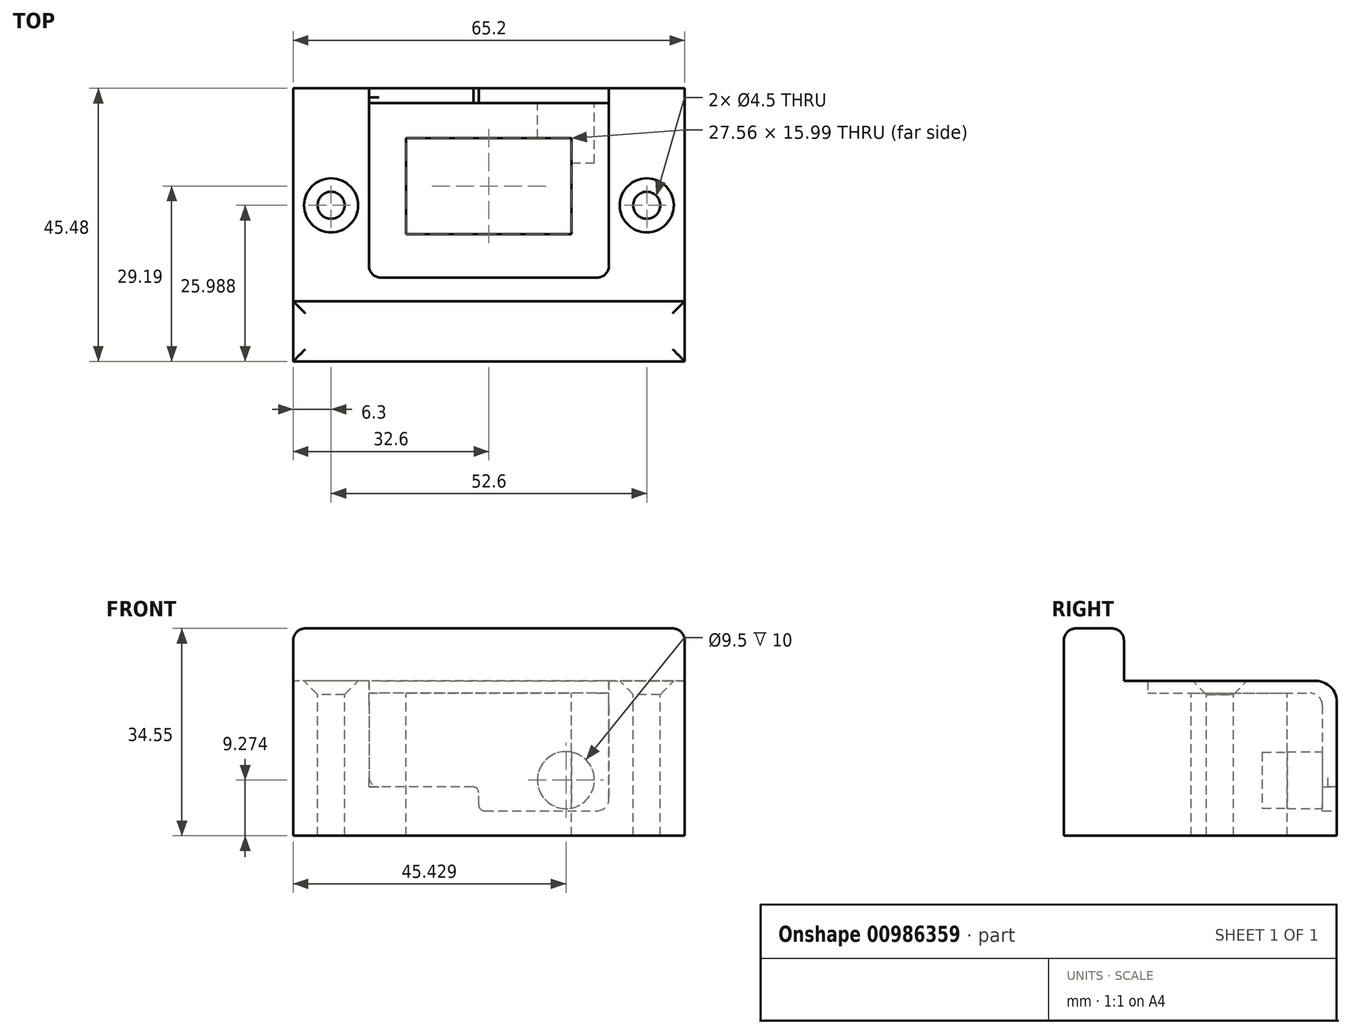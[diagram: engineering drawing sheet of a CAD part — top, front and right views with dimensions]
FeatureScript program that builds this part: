
annotation { "Feature Type Name" : "Feature", "Feature Type Description" : "" }
export const myFeature = defineFeature(function(context is Context, id is Id, definition is map)
    precondition{}
    {
        {
            var Q0;
            Q0=qCreatedBy(makeId("Right.planeOp"),FACE);
            var sketch = newSketch(context, id + "F0", { "sketchPlane" : qUnion([Q0])});
            skLineSegment(sketch, "E0.bottom", {"start": v(-15.25, 10.5) * mm, "end": v(15.25, 10.5) * mm});
            skLineSegment(sketch, "E0.top", {"start": v(13.85, -10.5) * mm, "end": v(15.25, -10.5) * mm});
            skLineSegment(sketch, "E0.left", {"start": v(-15.25, 10.5) * mm, "end": v(-15.25, 9.1) * mm});
            skLineSegment(sketch, "E0.right", {"start": v(15.25, 10.5) * mm, "end": v(15.25, -10.5) * mm});
            skPoint(sketch, "E0.middle", {"position": v(0, 0) * mm});
            skLineSegment(sketch, "E1.0", {"start": v(13.85, 9.1) * mm, "end": v(13.85, -10.5) * mm});
            skLineSegment(sketch, "E1.1", {"start": v(-15.25, 9.1) * mm, "end": v(13.85, 9.1) * mm});
            skPoint(sketch, "E2.orphan", {"position": v(-15.25, -10.5) * mm});
            skSolve(sketch);
        }
        {
            var Q0;
            Q0 = qSketchRegion(id + "F0", true);
            extrude(context, id + "F1", {"entities" : qUnion([Q0]), "endBound" : BoundingType.SYMMETRIC, "depth" : 40 * mm, "offsetDistance" : 25 * mm});
        }
        {
            var Q0;
            Q0=makeQuery(id+"F1.opExtrude","SWEPT_EDGE",EDGE,{"disambiguationData":[OSD([sQuery(id+"F0.wireOp",EDGE,"E1.0"),sQuery(id+"F0.wireOp",EDGE,"E1.1")])]});
            fillet(context, id + "F2", {"entities" : qUnion([Q0]), "radius" : 2 * mm, "tangentPropagation" : true, "allowEdgeOverflow" : false});
        }
        {
            var Q0;
            Q0=makeQuery(id+"F1.opExtrude","SWEPT_EDGE",EDGE,{"disambiguationData":[OSD([sQuery(id+"F0.wireOp",EDGE,"E0.bottom"),sQuery(id+"F0.wireOp",EDGE,"E0.right")])]});
            fillet(context, id + "F3", {"entities" : qUnion([Q0]), "radius" : 3 * mm, "tangentPropagation" : true, "allowEdgeOverflow" : false});
        }
        {
            var Q0;
            Q0=makeQuery(id+"F1.opExtrude","CAP_EDGE",EDGE,{"disambiguationData":[OSD([sQuery(id+"F0.wireOp",EDGE,"E0.top")])],"isStart":false});
            var Q1;
            Q1=makeQuery(id+"F1.opExtrude","CAP_EDGE",EDGE,{"disambiguationData":[OSD([sQuery(id+"F0.wireOp",EDGE,"E0.left")])],"isStart":false});
            var Q2;
            Q2=makeQuery(id+"F1.opExtrude","CAP_EDGE",EDGE,{"disambiguationData":[OSD([sQuery(id+"F0.wireOp",EDGE,"E0.left")])],"isStart":true});
            fillet(context, id + "F4", {"entities" : qUnion([Q0, Q1, Q2]), "radius" : 2 * mm, "tangentPropagation" : true, "allowEdgeOverflow" : false});
        }
        {
            var Q0;
            Q0=makeQuery(id+"F1.opExtrude","SWEPT_FACE",FACE,{"disambiguationData":[OSD([sQuery(id+"F0.wireOp",EDGE,"E0.right")])]});
            var sketch = newSketch(context, id + "F5", { "sketchPlane" : qUnion([Q0])});
            skLineSegment(sketch, "E3", {"start": v(20, -10.5) * mm, "end": v(0, -10.5) * mm});
            skLineSegment(sketch, "E4", {"start": v(0, -10.5) * mm, "end": v(0, -6.5) * mm});
            skLineSegment(sketch, "E5", {"start": v(0, -6.5) * mm, "end": v(20, -6.5) * mm});
            skLineSegment(sketch, "E6", {"start": v(20, -6.5) * mm, "end": v(20, -10.5) * mm});
            skSolve(sketch);
        }
        {
            var Q0;
            Q0 = qSketchRegion(id + "F5", true);
            extrude(context, id + "F6", {"entities" : qUnion([Q0]), "operationType" : NewBodyOperationType.REMOVE, "oppositeDirection" : true, "depth" : 8.3 * mm, "offsetDistance" : 25 * mm});
        }
        {
            var Q0;
            Q0=makeQuery(id+"F6.boolean.opBoolean","COPY",EDGE,{"derivedFrom":makeQuery(id+"F6.opExtrude","SWEPT_EDGE",EDGE,{"disambiguationData":[OSD([sQuery(id+"F0.wireOp",EDGE,"E0.right"),sQuery(id+"F5.wireOp",EDGE,"E5"),sQuery(id+"F5.wireOp",EDGE,"E6")])]})});
            var Q1;
            Q1=makeQuery(id+"F6.boolean.opBoolean","COPY",EDGE,{"derivedFrom":makeQuery(id+"F6.opExtrude","SWEPT_EDGE",EDGE,{"disambiguationData":[OSD([sQuery(id+"F0.wireOp",EDGE,"E0.top"),sQuery(id+"F0.wireOp",EDGE,"E0.right"),sQuery(id+"F5.wireOp",EDGE,"E3"),sQuery(id+"F5.wireOp",EDGE,"E4")])]})});
            var Q2;
            Q2=makeQuery(id+"F6.boolean.opBoolean","COPY",EDGE,{"derivedFrom":makeQuery(id+"F6.opExtrude","SWEPT_EDGE",EDGE,{"disambiguationData":[OSD([sQuery(id+"F5.wireOp",EDGE,"E4"),sQuery(id+"F5.wireOp",EDGE,"E5")])]})});
            fillet(context, id + "F7", {"entities" : qUnion([Q0, Q1, Q2]), "radius" : 1.69 * mm, "tangentPropagation" : true, "allowEdgeOverflow" : false});
        }
        {
            var Q0;
            Q0=qCreatedBy(makeId("Right.planeOp"),FACE);
            var sketch = newSketch(context, id + "F8", { "sketchPlane" : qUnion([Q0])});
            skLineSegment(sketch, "E7.bottom", {"start": v(-14.79, 9.63) * mm, "end": v(12.79, 9.63) * mm});
            skLineSegment(sketch, "E7.right", {"start": v(14.79, 7.63) * mm, "end": v(14.79, -9.63) * mm});
            skPoint(sketch, "E7.middle", {"position": v(0, 0) * mm});
            skPoint(sketch, "E8.visualSharp", {"position": v(14.79, 9.63) * mm});
            skArc(sketch, "E8.filletArc", {"start": v(14.79, 7.63) * mm, "mid": v(14.2, 9.05) * mm, "end": v(12.79, 9.63) * mm});
            skLineSegment(sketch, "E9", {"start": v(-14.79, 9.63) * mm, "end": v(-16.56, 9.63) * mm});
            skLineSegment(sketch, "E10", {"start": v(-16.56, 9.63) * mm, "end": v(-16.56, -14.66) * mm});
            skLineSegment(sketch, "E11", {"start": v(-16.56, -14.66) * mm, "end": v(14.79, -14.66) * mm});
            skLineSegment(sketch, "E12", {"start": v(14.79, -14.66) * mm, "end": v(14.79, -9.63) * mm});
            skPoint(sketch, "E7.top.start.orphan", {"position": v(-14.79, -9.63) * mm});
            skSolve(sketch);
        }
        {
            var Q0;
            Q0=makeQuery(id+"F8.imprint","IMPRINT",FACE,{"disambiguationData":[TD([[makeQuery(id+"F8.imprint","IMPRINT",EDGE,{"derivedFrom":sQuery(id+"F8.wireOp",EDGE,"E7.bottom")}),-1.0]])]});
            extrude(context, id + "F9", {"entities" : qUnion([Q0]), "endBound" : BoundingType.SYMMETRIC, "depth" : 55.2 * mm, "offsetDistance" : 25 * mm});
        }
        {
            var Q0;
            Q0=makeQuery(id+"F1.opExtrude","SWEPT_BODY",BODY,{"disambiguationData":[OSD([sQuery(id+"F0.wireOp",EDGE,"E0.bottom"),sQuery(id+"F0.wireOp",EDGE,"E0.top"),sQuery(id+"F0.wireOp",EDGE,"E0.left"),sQuery(id+"F0.wireOp",EDGE,"E0.right"),sQuery(id+"F0.wireOp",EDGE,"E1.0"),sQuery(id+"F0.wireOp",EDGE,"E1.1")])]});
            var Q1;
            Q1=makeQuery(id+"F9.opExtrude","SWEPT_BODY",BODY,{"disambiguationData":[OSD([sQuery(id+"F8.wireOp",EDGE,"E7.bottom"),sQuery(id+"F8.wireOp",EDGE,"E7.right"),sQuery(id+"F8.wireOp",EDGE,"E8.filletArc"),sQuery(id+"F8.wireOp",EDGE,"E9"),sQuery(id+"F8.wireOp",EDGE,"E10"),sQuery(id+"F8.wireOp",EDGE,"E11"),sQuery(id+"F8.wireOp",EDGE,"E12")])]});
            booleanBodies(context, id + "F10", {"operationType" : BooleanOperationType.SUBTRACTION, "tools" : qUnion([Q0]), "targets" : qUnion([Q1])});
        }
        {
            var Q0;
            Q0=makeQuery(id+"F10.opBoolean","COPY",FACE,{"derivedFrom":makeQuery(id+"F1.opExtrude","SWEPT_FACE",FACE,{"disambiguationData":[OSD([sQuery(id+"F0.wireOp",EDGE,"E1.0")])]})});
            var sketch = newSketch(context, id + "F11", { "sketchPlane" : qUnion([Q0])});
            skLineSegment(sketch, "E13", {"start": v(-20, -6) * mm, "end": v(-13.75, -6) * mm});
            skPoint(sketch, "E14.end.orphan", {"position": v(-9.84, -6) * mm});
            skPoint(sketch, "E14.start.orphan", {"position": v(-9.84, -10.5) * mm});
            skSolve(sketch);
        }
        {
            var Q0;
            {var subQ0=sQuery(id+"F0.wireOp",EDGE,"E1.0");Q0=makeQuery(id+"F11.imprint","IMPRINT",FACE,{"disambiguationData":[TD([[makeQuery(id+"F11.imprint","IMPRINT",EDGE,{"derivedFrom":makeQuery(id+"F10.opBoolean","COPY",EDGE,{"derivedFrom":makeQuery(id+"F1.opExtrude","CAP_EDGE",EDGE,{"disambiguationData":[OSD([subQ0])],"isStart":true})})}),-1.0]])]});}
            var sketch = newSketch(context, id + "F12", { "sketchPlane" : qUnion([Q0])});
            skCircle(sketch, "E15", {"center": v(-12.83, -5.39) * mm, "radius": 4.75 * mm});
            skSolve(sketch);
        }
        {
            var Q0;
            Q0 = qSketchRegion(id + "F12", true);
            extrude(context, id + "F13", {"entities" : qUnion([Q0]), "operationType" : NewBodyOperationType.REMOVE, "oppositeDirection" : true, "depth" : 10 * mm, "offsetDistance" : 25 * mm});
        }
        {
            var Q0;
            Q0=makeQuery(id+"F9.opExtrude","CAP_FACE",FACE,{"disambiguationData":[OSD([sQuery(id+"F8.wireOp",EDGE,"E7.bottom"),sQuery(id+"F8.wireOp",EDGE,"E7.right"),sQuery(id+"F8.wireOp",EDGE,"E8.filletArc"),sQuery(id+"F8.wireOp",EDGE,"E9"),sQuery(id+"F8.wireOp",EDGE,"E10"),sQuery(id+"F8.wireOp",EDGE,"E11"),sQuery(id+"F8.wireOp",EDGE,"E12")])],"isStart":false});
            var sketch = newSketch(context, id + "F14", { "sketchPlane" : qUnion([Q0])});
            skLineSegment(sketch, "E16.0", {"start": v(16.29, 7.63) * mm, "end": v(16.29, -14.66) * mm});
            skArc(sketch, "E16.1", {"start": v(16.29, 7.63) * mm, "mid": v(15.26, 10.1) * mm, "end": v(12.79, 11.13) * mm});
            skLineSegment(sketch, "E16.2", {"start": v(-16.56, 11.13) * mm, "end": v(12.79, 11.13) * mm});
            skLineSegment(sketch, "E17", {"start": v(-16.56, 11.13) * mm, "end": v(-16.56, -14.66) * mm});
            skLineSegment(sketch, "E18", {"start": v(-16.56, -14.66) * mm, "end": v(16.29, -14.66) * mm});
            skSolve(sketch);
        }
        {
            var Q0;
            Q0 = qSketchRegion(id + "F14", true);
            var Q1;
            Q1=makeQuery(id+"F10.opBoolean","COPY",FACE,{"derivedFrom":makeQuery(id+"F1.opExtrude","CAP_FACE",FACE,{"disambiguationData":[OSD([sQuery(id+"F0.wireOp",EDGE,"E0.bottom"),sQuery(id+"F0.wireOp",EDGE,"E0.top"),sQuery(id+"F0.wireOp",EDGE,"E0.left"),sQuery(id+"F0.wireOp",EDGE,"E0.right"),sQuery(id+"F0.wireOp",EDGE,"E1.0"),sQuery(id+"F0.wireOp",EDGE,"E1.1")])],"isStart":false})});
            extrude(context, id + "F15", {"entities" : qUnion([Q0]), "operationType" : NewBodyOperationType.ADD, "endBound" : BoundingType.UP_TO_SURFACE, "oppositeDirection" : true, "depth" : 25 * mm, "endBoundEntityFace" : qUnion([Q1]), "offsetDistance" : 25 * mm});
        }
        {
            var Q0;
            Q0=makeQuery(id+"F9.opExtrude","CAP_FACE",FACE,{"disambiguationData":[OSD([sQuery(id+"F8.wireOp",EDGE,"E7.bottom"),sQuery(id+"F8.wireOp",EDGE,"E7.right"),sQuery(id+"F8.wireOp",EDGE,"E8.filletArc"),sQuery(id+"F8.wireOp",EDGE,"E9"),sQuery(id+"F8.wireOp",EDGE,"E10"),sQuery(id+"F8.wireOp",EDGE,"E11"),sQuery(id+"F8.wireOp",EDGE,"E12")])],"isStart":true});
            var sketch = newSketch(context, id + "F16", { "sketchPlane" : qUnion([Q0])});
            skLineSegment(sketch, "E19.0", {"start": v(-16.29, 7.63) * mm, "end": v(-16.29, -14.66) * mm});
            skArc(sketch, "E19.1", {"start": v(-16.29, 7.63) * mm, "mid": v(-15.26, 10.1) * mm, "end": v(-12.79, 11.13) * mm});
            skLineSegment(sketch, "E19.2", {"start": v(16.56, 11.13) * mm, "end": v(-12.79, 11.13) * mm});
            skLineSegment(sketch, "E20", {"start": v(16.56, 11.13) * mm, "end": v(16.56, -14.66) * mm});
            skLineSegment(sketch, "E21", {"start": v(16.56, -14.66) * mm, "end": v(-16.29, -14.66) * mm});
            skSolve(sketch);
        }
        {
            var Q0;
            Q0 = qSketchRegion(id + "F16", true);
            var Q1;
            Q1=makeQuery(id+"F10.opBoolean","COPY",FACE,{"derivedFrom":makeQuery(id+"F1.opExtrude","CAP_FACE",FACE,{"disambiguationData":[OSD([sQuery(id+"F0.wireOp",EDGE,"E0.bottom"),sQuery(id+"F0.wireOp",EDGE,"E0.top"),sQuery(id+"F0.wireOp",EDGE,"E0.left"),sQuery(id+"F0.wireOp",EDGE,"E0.right"),sQuery(id+"F0.wireOp",EDGE,"E1.0"),sQuery(id+"F0.wireOp",EDGE,"E1.1")])],"isStart":true})});
            extrude(context, id + "F17", {"entities" : qUnion([Q0]), "operationType" : NewBodyOperationType.ADD, "endBound" : BoundingType.UP_TO_SURFACE, "oppositeDirection" : true, "depth" : 25 * mm, "endBoundEntityFace" : qUnion([Q1]), "offsetDistance" : 25 * mm});
        }
        {
            var Q0;
            Q0=makeQuery(id+"F9.opExtrude","SWEPT_FACE",FACE,{"disambiguationData":[OSD([sQuery(id+"F8.wireOp",EDGE,"E7.bottom"),sQuery(id+"F8.wireOp",EDGE,"E9")])]});
            var sketch = newSketch(context, id + "F18", { "sketchPlane" : qUnion([Q0])});
            skLineSegment(sketch, "E22.bottom", {"start": v(20, -16.56) * mm, "end": v(-20, -16.56) * mm});
            skLineSegment(sketch, "E22.left", {"start": v(20, -16.56) * mm, "end": v(20, -13.25) * mm});
            skLineSegment(sketch, "E22.right", {"start": v(-20, -16.56) * mm, "end": v(-20, -13.25) * mm});
            skArc(sketch, "E23", {"start": v(18, -15.25) * mm, "mid": v(19.41, -14.66) * mm, "end": v(20, -13.25) * mm});
            skLineSegment(sketch, "E24", {"start": v(18, -15.25) * mm, "end": v(-18, -15.25) * mm});
            skArc(sketch, "E25", {"start": v(-20, -13.25) * mm, "mid": v(-19.41, -14.66) * mm, "end": v(-18, -15.25) * mm});
            skSolve(sketch);
        }
        {
            var Q0;
            Q0 = qSketchRegion(id + "F18", true);
            var Q1;
            Q1=makeQuery(id+"F15.opExtrude","SWEPT_FACE",FACE,{"disambiguationData":[OSD([sQuery(id+"F14.wireOp",EDGE,"E16.2")])]});
            extrude(context, id + "F19", {"entities" : qUnion([Q0]), "operationType" : NewBodyOperationType.ADD, "endBound" : BoundingType.UP_TO_SURFACE, "depth" : 25 * mm, "endBoundEntityFace" : qUnion([Q1]), "offsetDistance" : 25 * mm});
        }
        {
            var Q0;
            Q0=makeQuery(id+"F9.opExtrude","SWEPT_FACE",FACE,{"disambiguationData":[OSD([sQuery(id+"F8.wireOp",EDGE,"E7.right"),sQuery(id+"F8.wireOp",EDGE,"E12")])]});
            var sketch = newSketch(context, id + "F20", { "sketchPlane" : qUnion([Q0])});
            skLineSegment(sketch, "E26.bottom", {"start": v(-20, -14.66) * mm, "end": v(20, -14.66) * mm});
            skLineSegment(sketch, "E26.left", {"start": v(-20, -14.66) * mm, "end": v(-20, -8.5) * mm});
            skLineSegment(sketch, "E26.right", {"start": v(20, -14.66) * mm, "end": v(20, -4.81) * mm});
            skArc(sketch, "E27", {"start": v(-20, -8.5) * mm, "mid": v(-19.41, -9.91) * mm, "end": v(-18, -10.5) * mm});
            skArc(sketch, "E28", {"start": v(-1.69, -10.5) * mm, "mid": v(-0.5, -10) * mm, "end": v(0, -8.81) * mm});
            skArc(sketch, "E29", {"start": v(1.69, -6.5) * mm, "mid": v(0.5, -7) * mm, "end": v(0, -8.19) * mm});
            skLineSegment(sketch, "E30", {"start": v(0, -8.19) * mm, "end": v(0, -8.81) * mm});
            skArc(sketch, "E31", {"start": v(18.31, -6.5) * mm, "mid": v(19.5, -6) * mm, "end": v(20, -4.81) * mm});
            skLineSegment(sketch, "E32", {"start": v(1.69, -6.5) * mm, "end": v(18.31, -6.5) * mm});
            skLineSegment(sketch, "E33", {"start": v(-18, -10.5) * mm, "end": v(-1.69, -10.5) * mm});
            skSolve(sketch);
        }
        {
            var Q0;
            Q0 = qSketchRegion(id + "F20", true);
            var Q1;
            Q1=makeQuery(id+"F17.opExtrude","SWEPT_FACE",FACE,{"disambiguationData":[OSD([sQuery(id+"F16.wireOp",EDGE,"E19.0")])]});
            extrude(context, id + "F21", {"entities" : qUnion([Q0]), "operationType" : NewBodyOperationType.ADD, "endBound" : BoundingType.UP_TO_SURFACE, "depth" : 25 * mm, "endBoundEntityFace" : qUnion([Q1]), "offsetDistance" : 25 * mm});
        }
        {
            var Q0;
            Q0=makeQuery(id+"F17.boolean.opBoolean","MERGE",FACE,{"derivedFrom":[makeQuery(id+"F9.opExtrude","CAP_FACE",FACE,{"disambiguationData":[OSD([sQuery(id+"F8.wireOp",EDGE,"E7.bottom"),sQuery(id+"F8.wireOp",EDGE,"E7.right"),sQuery(id+"F8.wireOp",EDGE,"E8.filletArc"),sQuery(id+"F8.wireOp",EDGE,"E9"),sQuery(id+"F8.wireOp",EDGE,"E10"),sQuery(id+"F8.wireOp",EDGE,"E11"),sQuery(id+"F8.wireOp",EDGE,"E12")])],"isStart":true}),makeQuery(id+"F17.opExtrude","CAP_FACE",FACE,{"disambiguationData":[OSD([sQuery(id+"F16.wireOp",EDGE,"E19.0"),sQuery(id+"F16.wireOp",EDGE,"E19.1"),sQuery(id+"F16.wireOp",EDGE,"E19.2"),sQuery(id+"F16.wireOp",EDGE,"E20"),sQuery(id+"F16.wireOp",EDGE,"E21")])],"isStart":true})]});
            var sketch = newSketch(context, id + "F22", { "sketchPlane" : qUnion([Q0])});
            skLineSegment(sketch, "E34.bottom", {"start": v(16.56, -14.66) * mm, "end": v(-16.29, -14.66) * mm});
            skLineSegment(sketch, "E34.top", {"start": v(16.56, 11.13) * mm, "end": v(-12.79, 11.13) * mm});
            skLineSegment(sketch, "E34.left", {"start": v(16.56, -14.66) * mm, "end": v(16.56, 11.13) * mm});
            skLineSegment(sketch, "E34.right", {"start": v(-16.29, -14.66) * mm, "end": v(-16.29, 7.63) * mm});
            skPoint(sketch, "E35.visualSharp", {"position": v(-16.29, 11.13) * mm});
            skArc(sketch, "E35.filletArc", {"start": v(-12.79, 11.13) * mm, "mid": v(-15.26, 10.1) * mm, "end": v(-16.29, 7.63) * mm});
            skSolve(sketch);
        }
        {
            var Q0;
            Q0 = qSketchRegion(id + "F22", true);
            extrude(context, id + "F23", {"entities" : qUnion([Q0]), "operationType" : NewBodyOperationType.ADD, "depth" : 5 * mm, "offsetDistance" : 25 * mm});
        }
        {
            var Q0;
            Q0=makeQuery(id+"F15.boolean.opBoolean","MERGE",FACE,{"derivedFrom":[makeQuery(id+"F9.opExtrude","CAP_FACE",FACE,{"disambiguationData":[OSD([sQuery(id+"F8.wireOp",EDGE,"E7.bottom"),sQuery(id+"F8.wireOp",EDGE,"E7.right"),sQuery(id+"F8.wireOp",EDGE,"E8.filletArc"),sQuery(id+"F8.wireOp",EDGE,"E9"),sQuery(id+"F8.wireOp",EDGE,"E10"),sQuery(id+"F8.wireOp",EDGE,"E11"),sQuery(id+"F8.wireOp",EDGE,"E12")])],"isStart":false}),makeQuery(id+"F15.opExtrude","CAP_FACE",FACE,{"disambiguationData":[OSD([sQuery(id+"F14.wireOp",EDGE,"E16.0"),sQuery(id+"F14.wireOp",EDGE,"E16.1"),sQuery(id+"F14.wireOp",EDGE,"E16.2"),sQuery(id+"F14.wireOp",EDGE,"E17"),sQuery(id+"F14.wireOp",EDGE,"E18")])],"isStart":true})]});
            var sketch = newSketch(context, id + "F24", { "sketchPlane" : qUnion([Q0])});
            skLineSegment(sketch, "E36.bottom", {"start": v(-16.56, -14.66) * mm, "end": v(16.29, -14.66) * mm});
            skLineSegment(sketch, "E36.top", {"start": v(-16.56, 11.13) * mm, "end": v(12.79, 11.13) * mm});
            skLineSegment(sketch, "E36.left", {"start": v(-16.56, -14.66) * mm, "end": v(-16.56, 11.13) * mm});
            skLineSegment(sketch, "E36.right", {"start": v(16.29, -14.66) * mm, "end": v(16.29, 7.63) * mm});
            skPoint(sketch, "E37.visualSharp", {"position": v(16.29, 11.13) * mm});
            skArc(sketch, "E37.filletArc", {"start": v(16.29, 7.63) * mm, "mid": v(15.26, 10.1) * mm, "end": v(12.79, 11.13) * mm});
            skSolve(sketch);
        }
        {
            var Q0;
            Q0 = qSketchRegion(id + "F24", true);
            extrude(context, id + "F25", {"entities" : qUnion([Q0]), "operationType" : NewBodyOperationType.ADD, "depth" : 5 * mm, "offsetDistance" : 25 * mm});
        }
        {
            var Q0;
            Q0=makeQuery(id+"F25.boolean.opBoolean","MERGE",FACE,{"derivedFrom":[makeQuery(id+"F23.boolean.opBoolean","MERGE",FACE,{"derivedFrom":[makeQuery(id+"F21.boolean.opBoolean","MERGE",FACE,{"derivedFrom":[makeQuery(id+"F15.opExtrude","SWEPT_FACE",FACE,{"disambiguationData":[OSD([sQuery(id+"F14.wireOp",EDGE,"E16.0")])]}),makeQuery(id+"F17.opExtrude","SWEPT_FACE",FACE,{"disambiguationData":[OSD([sQuery(id+"F16.wireOp",EDGE,"E19.0")])]}),makeQuery(id+"F21.opExtrude","CAP_FACE",FACE,{"disambiguationData":[OSD([sQuery(id+"F20.wireOp",EDGE,"E26.bottom"),sQuery(id+"F20.wireOp",EDGE,"E26.left"),sQuery(id+"F20.wireOp",EDGE,"E26.right"),sQuery(id+"F20.wireOp",EDGE,"E27"),sQuery(id+"F20.wireOp",EDGE,"E28"),sQuery(id+"F20.wireOp",EDGE,"E29"),sQuery(id+"F20.wireOp",EDGE,"E30"),sQuery(id+"F20.wireOp",EDGE,"E31"),sQuery(id+"F20.wireOp",EDGE,"E32"),sQuery(id+"F20.wireOp",EDGE,"E33")])],"isStart":false})]}),makeQuery(id+"F23.opExtrude","SWEPT_FACE",FACE,{"disambiguationData":[OSD([sQuery(id+"F22.wireOp",EDGE,"E34.right")])]})]}),makeQuery(id+"F25.opExtrude","SWEPT_FACE",FACE,{"disambiguationData":[OSD([sQuery(id+"F24.wireOp",EDGE,"E36.right")])]})]});
            var sketch = newSketch(context, id + "F26", { "sketchPlane" : qUnion([Q0])});
            skLineSegment(sketch, "E38.1", {"start": v(1.7, -8.11) * mm, "end": v(1.7, -7.5) * mm});
            skLineSegment(sketch, "E39", {"start": v(-1.69, -10.5) * mm, "end": v(0.7, -10.5) * mm});
            skLineSegment(sketch, "E40", {"start": v(1.7, -9.5) * mm, "end": v(1.7, -8.11) * mm});
            skPoint(sketch, "E41.visualSharp", {"position": v(1.7, -10.5) * mm});
            skArc(sketch, "E41.filletArc", {"start": v(0.7, -10.5) * mm, "mid": v(1.42, -10.2) * mm, "end": v(1.7, -9.5) * mm});
            skPoint(sketch, "E42.start.orphan", {"position": v(1.8, -6.5) * mm});
            skArc(sketch, "E43", {"start": v(2.85, -6.5) * mm, "mid": v(2.05, -6.74) * mm, "end": v(1.7, -7.5) * mm});
            skLineSegment(sketch, "E44", {"start": v(-1.69, -10.5) * mm, "end": v(-1.69, -6.5) * mm});
            skLineSegment(sketch, "E45", {"start": v(-1.69, -6.5) * mm, "end": v(2.85, -6.5) * mm});
            skSolve(sketch);
        }
        {
            var Q0;
            Q0 = qSketchRegion(id + "F26", true);
            var Q1;
            Q1=makeQuery(id+"F10.opBoolean","COPY",FACE,{"derivedFrom":makeQuery(id+"F1.opExtrude","SWEPT_FACE",FACE,{"disambiguationData":[OSD([sQuery(id+"F0.wireOp",EDGE,"E1.0")])]})});
            extrude(context, id + "F27", {"entities" : qUnion([Q0]), "operationType" : NewBodyOperationType.REMOVE, "endBound" : BoundingType.UP_TO_SURFACE, "oppositeDirection" : true, "depth" : 25 * mm, "endBoundEntityFace" : qUnion([Q1]), "offsetDistance" : 25 * mm});
        }
        {
            var Q0;
            Q0=makeQuery(id+"F25.boolean.opBoolean","MERGE",FACE,{"derivedFrom":[makeQuery(id+"F23.boolean.opBoolean","MERGE",FACE,{"derivedFrom":[makeQuery(id+"F19.boolean.opBoolean","MERGE",FACE,{"derivedFrom":[makeQuery(id+"F15.opExtrude","SWEPT_FACE",FACE,{"disambiguationData":[OSD([sQuery(id+"F14.wireOp",EDGE,"E16.2")])]}),makeQuery(id+"F17.opExtrude","SWEPT_FACE",FACE,{"disambiguationData":[OSD([sQuery(id+"F16.wireOp",EDGE,"E19.2")])]}),makeQuery(id+"F19.opExtrude","CAP_FACE",FACE,{"disambiguationData":[OSD([sQuery(id+"F18.wireOp",EDGE,"E22.bottom"),sQuery(id+"F18.wireOp",EDGE,"E22.left"),sQuery(id+"F18.wireOp",EDGE,"E22.right"),sQuery(id+"F18.wireOp",EDGE,"E23"),sQuery(id+"F18.wireOp",EDGE,"E24"),sQuery(id+"F18.wireOp",EDGE,"E25")])],"isStart":false})]}),makeQuery(id+"F23.opExtrude","SWEPT_FACE",FACE,{"disambiguationData":[OSD([sQuery(id+"F22.wireOp",EDGE,"E34.top")])]})]}),makeQuery(id+"F25.opExtrude","SWEPT_FACE",FACE,{"disambiguationData":[OSD([sQuery(id+"F24.wireOp",EDGE,"E36.top")])]})]});
            var sketch = newSketch(context, id + "F28", { "sketchPlane" : qUnion([Q0])});
            skLineSegment(sketch, "E46.bottom", {"start": v(32.6, -16.56) * mm, "end": v(-32.6, -16.56) * mm});
            skLineSegment(sketch, "E46.top", {"start": v(32.6, -19.2) * mm, "end": v(-32.6, -19.2) * mm});
            skLineSegment(sketch, "E46.left", {"start": v(32.6, -16.56) * mm, "end": v(32.6, -19.2) * mm});
            skLineSegment(sketch, "E46.right", {"start": v(-32.6, -16.56) * mm, "end": v(-32.6, -19.2) * mm});
            skSolve(sketch);
        }
        {
            var Q0;
            Q0 = qSketchRegion(id + "F28", true);
            var Q1;
            Q1=makeQuery(id+"F25.boolean.opBoolean","MERGE",FACE,{"derivedFrom":[makeQuery(id+"F23.boolean.opBoolean","MERGE",FACE,{"derivedFrom":[makeQuery(id+"F21.boolean.opBoolean","MERGE",FACE,{"derivedFrom":[makeQuery(id+"F17.boolean.opBoolean","MERGE",FACE,{"derivedFrom":[makeQuery(id+"F15.boolean.opBoolean","MERGE",FACE,{"derivedFrom":[makeQuery(id+"F9.opExtrude","SWEPT_FACE",FACE,{"disambiguationData":[OSD([sQuery(id+"F8.wireOp",EDGE,"E11")])]}),makeQuery(id+"F15.opExtrude","SWEPT_FACE",FACE,{"disambiguationData":[OSD([sQuery(id+"F14.wireOp",EDGE,"E18")])]})]}),makeQuery(id+"F17.opExtrude","SWEPT_FACE",FACE,{"disambiguationData":[OSD([sQuery(id+"F16.wireOp",EDGE,"E21")])]})]}),makeQuery(id+"F21.opExtrude","SWEPT_FACE",FACE,{"disambiguationData":[OSD([sQuery(id+"F20.wireOp",EDGE,"E26.bottom")])]})]}),makeQuery(id+"F23.opExtrude","SWEPT_FACE",FACE,{"disambiguationData":[OSD([sQuery(id+"F22.wireOp",EDGE,"E34.bottom")])]})]}),makeQuery(id+"F25.opExtrude","SWEPT_FACE",FACE,{"disambiguationData":[OSD([sQuery(id+"F24.wireOp",EDGE,"E36.bottom")])]})]});
            extrude(context, id + "F29", {"entities" : qUnion([Q0]), "operationType" : NewBodyOperationType.ADD, "endBound" : BoundingType.UP_TO_SURFACE, "oppositeDirection" : true, "depth" : 25 * mm, "endBoundEntityFace" : qUnion([Q1]), "offsetDistance" : 25 * mm});
        }
        {
            var Q0;
            Q0=makeQuery(id+"F29.boolean.opBoolean","MERGE",FACE,{"derivedFrom":[makeQuery(id+"F25.boolean.opBoolean","MERGE",FACE,{"derivedFrom":[makeQuery(id+"F23.boolean.opBoolean","MERGE",FACE,{"derivedFrom":[makeQuery(id+"F19.boolean.opBoolean","MERGE",FACE,{"derivedFrom":[makeQuery(id+"F15.opExtrude","SWEPT_FACE",FACE,{"disambiguationData":[OSD([sQuery(id+"F14.wireOp",EDGE,"E16.2")])]}),makeQuery(id+"F17.opExtrude","SWEPT_FACE",FACE,{"disambiguationData":[OSD([sQuery(id+"F16.wireOp",EDGE,"E19.2")])]}),makeQuery(id+"F19.opExtrude","CAP_FACE",FACE,{"disambiguationData":[OSD([sQuery(id+"F18.wireOp",EDGE,"E22.bottom"),sQuery(id+"F18.wireOp",EDGE,"E22.left"),sQuery(id+"F18.wireOp",EDGE,"E22.right"),sQuery(id+"F18.wireOp",EDGE,"E23"),sQuery(id+"F18.wireOp",EDGE,"E24"),sQuery(id+"F18.wireOp",EDGE,"E25")])],"isStart":false})]}),makeQuery(id+"F23.opExtrude","SWEPT_FACE",FACE,{"disambiguationData":[OSD([sQuery(id+"F22.wireOp",EDGE,"E34.top")])]})]}),makeQuery(id+"F25.opExtrude","SWEPT_FACE",FACE,{"disambiguationData":[OSD([sQuery(id+"F24.wireOp",EDGE,"E36.top")])]})]}),makeQuery(id+"F29.opExtrude","CAP_FACE",FACE,{"disambiguationData":[OSD([sQuery(id+"F28.wireOp",EDGE,"E46.bottom"),sQuery(id+"F28.wireOp",EDGE,"E46.top"),sQuery(id+"F28.wireOp",EDGE,"E46.left"),sQuery(id+"F28.wireOp",EDGE,"E46.right")])],"isStart":true})]});
            var sketch = newSketch(context, id + "F30", { "sketchPlane" : qUnion([Q0])});
            skLineSegment(sketch, "E47", {"start": v(26.3, 12.79) * mm, "end": v(26.3, -19.2) * mm});
            skPoint(sketch, "E48", {"position": v(26.3, -3.2) * mm});
            skLineSegment(sketch, "E49", {"start": v(0, 0) * mm, "end": v(0, -23.13) * mm});
            skPoint(sketch, "E49.endSnap0", {"position": v(0, -19.2) * mm});
            skPoint(sketch, "E50.MirrorP", {"position": v(-26.3, -3.2) * mm});
            skSolve(sketch);
        }
        {
            var Q0;
            Q0=sQuery(id+"F30.wireOp",VERTEX,"E48");
            var Q1;
            Q1=sQuery(id+"F30.wireOp",VERTEX,"E50.MirrorP");
            var Q2;
            Q2=makeQuery(id+"F9.opExtrude","SWEPT_BODY",BODY,{"disambiguationData":[OSD([sQuery(id+"F8.wireOp",EDGE,"E7.bottom"),sQuery(id+"F8.wireOp",EDGE,"E7.right"),sQuery(id+"F8.wireOp",EDGE,"E8.filletArc"),sQuery(id+"F8.wireOp",EDGE,"E9"),sQuery(id+"F8.wireOp",EDGE,"E10"),sQuery(id+"F8.wireOp",EDGE,"E11"),sQuery(id+"F8.wireOp",EDGE,"E12")])]});
            hole(context, id + "F31", {"style" : HoleStyle.C_SINK, "endStyle" : HoleEndStyle.THROUGH, "standardTappedOrClearance" : lookupTablePath({ "standard" : "ISO", "size" : "4.5", "type" : "Drilled" }), "standardBlindInLast" : lookupTablePath({ "standard" : "ISO", "size" : "4.5", "type" : "Drilled" }), "holeDiameter" : 4.5 * mm, "cSinkDiameter" : 9 * mm, "cSinkAngle" : 90 * degree, "majorDiameter" : 5 * mm, "isTappedThrough" : true, "tappedDepth" : 12 * mm, "tapClearance" : 3, "locations" : qUnion([Q0, Q1]), "scope" : qUnion([Q2])});
        }
        {
            var Q0;
            Q0=makeQuery(id+"F10.opBoolean","COPY",FACE,{"derivedFrom":makeQuery(id+"F1.opExtrude","SWEPT_FACE",FACE,{"disambiguationData":[OSD([sQuery(id+"F0.wireOp",EDGE,"E1.1")])]})});
            var sketch = newSketch(context, id + "F32", { "sketchPlane" : qUnion([Q0])});
            skLineSegment(sketch, "E51", {"start": v(-20, -0.7) * mm, "end": v(0, -0.7) * mm});
            skLineSegment(sketch, "E52.bottom", {"start": v(-13.78, -8) * mm, "end": v(13.78, -8) * mm});
            skLineSegment(sketch, "E52.top", {"start": v(-13.78, 8) * mm, "end": v(13.78, 8) * mm});
            skLineSegment(sketch, "E52.left", {"start": v(-13.78, -8) * mm, "end": v(-13.78, 8) * mm});
            skLineSegment(sketch, "E52.right", {"start": v(13.78, -8) * mm, "end": v(13.78, 8) * mm});
            skPoint(sketch, "E52.middle", {"position": v(0, 0) * mm});
            skSolve(sketch);
        }
        {
            var Q0;
            Q0 = qSketchRegion(id + "F32", true);
            extrude(context, id + "F33", {"entities" : qUnion([Q0]), "operationType" : NewBodyOperationType.REMOVE, "oppositeDirection" : true, "depth" : 25 * mm, "offsetDistance" : 25 * mm});
        }
        {
            var Q0;
            Q0=makeQuery(id+"F29.opExtrude","SWEPT_FACE",FACE,{"disambiguationData":[OSD([sQuery(id+"F28.wireOp",EDGE,"E46.top")])]});
            var sketch = newSketch(context, id + "F34", { "sketchPlane" : qUnion([Q0])});
            skLineSegment(sketch, "E53.bottom", {"start": v(-32.6, -14.66) * mm, "end": v(32.6, -14.66) * mm});
            skLineSegment(sketch, "E53.top", {"start": v(-32.6, 19.89) * mm, "end": v(32.6, 19.89) * mm});
            skLineSegment(sketch, "E53.left", {"start": v(-32.6, -14.66) * mm, "end": v(-32.6, 19.89) * mm});
            skLineSegment(sketch, "E53.right", {"start": v(32.6, -14.66) * mm, "end": v(32.6, 19.89) * mm});
            skSolve(sketch);
        }
        {
            var Q0;
            Q0 = qSketchRegion(id + "F34", true);
            extrude(context, id + "F35", {"entities" : qUnion([Q0]), "operationType" : NewBodyOperationType.ADD, "depth" : 10 * mm, "offsetDistance" : 25 * mm});
        }
        {
            var Q0;
            Q0=makeQuery(id+"F35.opExtrude","SWEPT_EDGE",EDGE,{"disambiguationData":[OSD([sQuery(id+"F34.wireOp",EDGE,"E53.top"),sQuery(id+"F34.wireOp",EDGE,"E53.right")])]});
            var Q1;
            Q1=makeQuery(id+"F35.opExtrude","SWEPT_FACE",FACE,{"disambiguationData":[OSD([sQuery(id+"F34.wireOp",EDGE,"E53.top")])]});
            fillet(context, id + "F36", {"entities" : qUnion([Q0, Q1]), "radius" : 2 * mm, "tangentPropagation" : true, "allowEdgeOverflow" : false});
        }
    });
